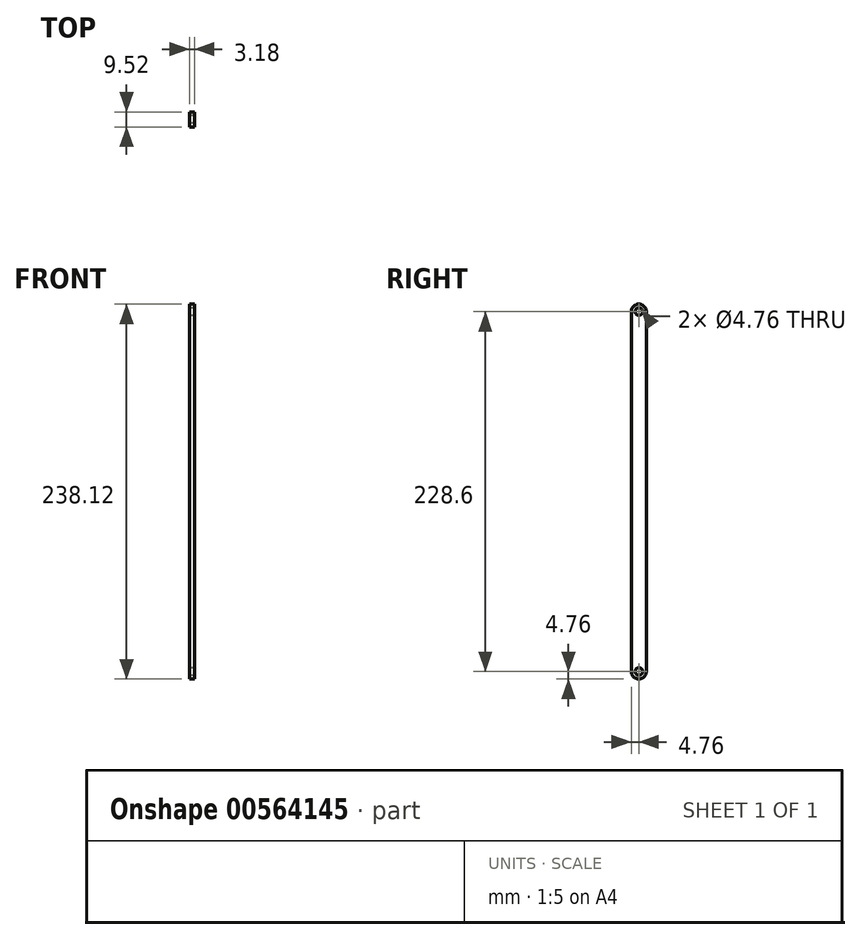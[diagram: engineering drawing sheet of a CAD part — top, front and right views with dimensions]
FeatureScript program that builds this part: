
annotation { "Feature Type Name" : "Feature", "Feature Type Description" : "" }
export const myFeature = defineFeature(function(context is Context, id is Id, definition is map)
    precondition{}
    {
        {
            var Q0;
            Q0=qCreatedBy(makeId("Right.planeOp"),FACE);
            var sketch = newSketch(context, id + "F0", { "sketchPlane" : qUnion([Q0])});
            skCircle(sketch, "E0", {"center": v(0, 0) * mm, "radius": 2.38 * mm});
            skCircle(sketch, "E1", {"center": v(0, 228.6) * mm, "radius": 2.38 * mm});
            skCircle(sketch, "E2", {"center": v(0, 228.6) * mm, "radius": 4.76 * mm});
            skCircle(sketch, "E3", {"center": v(0, 0) * mm, "radius": 4.76 * mm});
            skLineSegment(sketch, "E4", {"start": v(-4.76, 228.6) * mm, "end": v(-4.76, 0) * mm});
            skLineSegment(sketch, "E5", {"start": v(4.76, 228.6) * mm, "end": v(4.76, 0) * mm});
            skSolve(sketch);
        }
        {
            var Q0;
            Q0=qSketchRegion(id+"F0",true);
            extrude(context, id + "F1", {"entities" : qUnion([Q0]), "depth" : 3.17 * mm, "offsetDistance" : 25.4 * mm});
        }
    });
